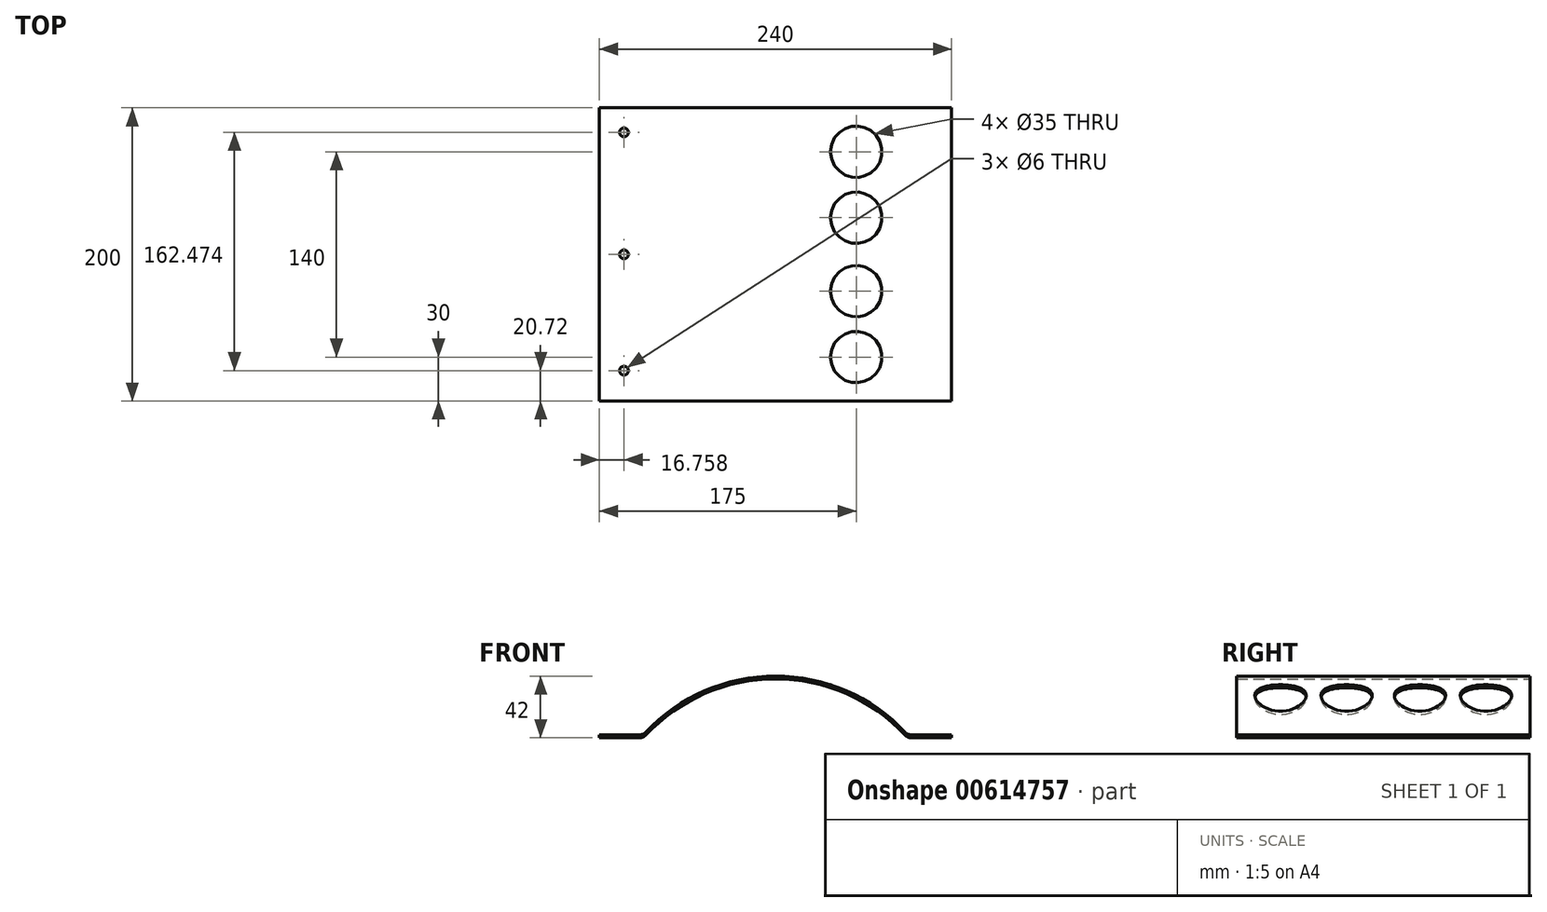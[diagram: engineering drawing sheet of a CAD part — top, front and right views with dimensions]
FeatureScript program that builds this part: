
annotation { "Feature Type Name" : "Feature", "Feature Type Description" : "" }
export const myFeature = defineFeature(function(context is Context, id is Id, definition is map)
    precondition{}
    {
        {
            var Q0;
            Q0=qCreatedBy(makeId("Front.planeOp"),FACE);
            var sketch = newSketch(context, id + "F0", { "sketchPlane" : qUnion([Q0])});
            skLineSegment(sketch, "E0", {"start": v(-120, 0) * mm, "end": v(-120, 2) * mm});
            skLineSegment(sketch, "E1", {"start": v(-120, 2) * mm, "end": v(-90, 2) * mm});
            skLineSegment(sketch, "E2", {"start": v(-90, 2) * mm, "end": v(-90, 0) * mm});
            skLineSegment(sketch, "E3", {"start": v(-90, 0) * mm, "end": v(-120, 0) * mm});
            skLineSegment(sketch, "E4", {"start": v(90, 0) * mm, "end": v(120, 0) * mm});
            skLineSegment(sketch, "E5", {"start": v(120, 0) * mm, "end": v(120, 2) * mm});
            skLineSegment(sketch, "E6", {"start": v(120, 2) * mm, "end": v(90, 2) * mm});
            skLineSegment(sketch, "E7", {"start": v(90, 2) * mm, "end": v(90, 0) * mm});
            skArc(sketch, "E8", {"start": v(90, 0) * mm, "mid": v(0, 40) * mm, "end": v(-90, 0) * mm});
            skArc(sketch, "E9", {"start": v(90, 2) * mm, "mid": v(0, 42) * mm, "end": v(-90, 2) * mm});
            skSolve(sketch);
        }
        {
            var Q0;
            Q0=makeQuery(id+"F0.imprint","IMPRINT",FACE,{"disambiguationData":[TD([[makeQuery(id+"F0.imprint","IMPRINT",EDGE,{"derivedFrom":sQuery(id+"F0.wireOp",EDGE,"E0")}),-1.0]])]});
            var Q1;
            Q1=makeQuery(id+"F0.imprint","IMPRINT",FACE,{"disambiguationData":[TD([[makeQuery(id+"F0.imprint","IMPRINT",EDGE,{"derivedFrom":sQuery(id+"F0.wireOp",EDGE,"E2")}),1.0]])]});
            var Q2;
            Q2=makeQuery(id+"F0.imprint","IMPRINT",FACE,{"disambiguationData":[TD([[makeQuery(id+"F0.imprint","IMPRINT",EDGE,{"derivedFrom":sQuery(id+"F0.wireOp",EDGE,"E4")}),1.0]])]});
            extrude(context, id + "F1", {"entities" : qUnion([Q0, Q1, Q2]), "depth" : 200 * mm, "offsetDistance" : 25 * mm});
        }
        {
            var Q0;
            Q0=makeQuery(id+"F1.opExtrude","SWEPT_FACE",FACE,{"disambiguationData":[OSD([sQuery(id+"F0.wireOp",EDGE,"E1")])]});
            var sketch = newSketch(context, id + "F2", { "sketchPlane" : qUnion([Q0])});
            skCircle(sketch, "E10", {"center": v(-103.24, -100) * mm, "radius": 3 * mm});
            skPoint(sketch, "E10.centerSnap0", {"position": v(-90, -100) * mm});
            skCircle(sketch, "E11", {"center": v(-103.24, -16.8) * mm, "radius": 3 * mm});
            skCircle(sketch, "E12", {"center": v(-103.24, -179.28) * mm, "radius": 3 * mm});
            skCircle(sketch, "E13", {"center": v(55, -30) * mm, "radius": 17.5 * mm});
            skCircle(sketch, "E14", {"center": v(55, -75) * mm, "radius": 17.5 * mm});
            skCircle(sketch, "E15", {"center": v(55, -125) * mm, "radius": 17.5 * mm});
            skCircle(sketch, "E16", {"center": v(55, -170) * mm, "radius": 17.5 * mm});
            skSolve(sketch);
        }
        {
            var Q0;
            Q0=makeQuery(id+"F2.imprint","IMPRINT",FACE,{"disambiguationData":[TD([[makeQuery(id+"F2.imprint","IMPRINT",EDGE,{"derivedFrom":sQuery(id+"F2.wireOp",EDGE,"E11")}),1.0]])]});
            var Q1;
            Q1=makeQuery(id+"F2.imprint","IMPRINT",FACE,{"disambiguationData":[TD([[makeQuery(id+"F2.imprint","IMPRINT",EDGE,{"derivedFrom":sQuery(id+"F2.wireOp",EDGE,"E10")}),1.0]])]});
            var Q2;
            Q2=makeQuery(id+"F2.imprint","IMPRINT",FACE,{"disambiguationData":[TD([[makeQuery(id+"F2.imprint","IMPRINT",EDGE,{"derivedFrom":sQuery(id+"F2.wireOp",EDGE,"E12")}),1.0]])]});
            extrude(context, id + "F3", {"entities" : qUnion([Q0, Q1, Q2]), "operationType" : NewBodyOperationType.REMOVE, "oppositeDirection" : true, "depth" : 25 * mm, "offsetDistance" : 25 * mm});
        }
        {
            var Q0;
            Q0=makeQuery(id+"F2.imprint","IMPRINT",FACE,{"disambiguationData":[TD([[makeQuery(id+"F2.imprint","IMPRINT",EDGE,{"derivedFrom":sQuery(id+"F2.wireOp",EDGE,"E13")}),1.0]])]});
            var Q1;
            Q1=makeQuery(id+"F2.imprint","IMPRINT",FACE,{"disambiguationData":[TD([[makeQuery(id+"F2.imprint","IMPRINT",EDGE,{"derivedFrom":sQuery(id+"F2.wireOp",EDGE,"E14")}),1.0]])]});
            var Q2;
            Q2=makeQuery(id+"F2.imprint","IMPRINT",FACE,{"disambiguationData":[TD([[makeQuery(id+"F2.imprint","IMPRINT",EDGE,{"derivedFrom":sQuery(id+"F2.wireOp",EDGE,"E15")}),1.0]])]});
            var Q3;
            Q3=makeQuery(id+"F2.imprint","IMPRINT",FACE,{"disambiguationData":[TD([[makeQuery(id+"F2.imprint","IMPRINT",EDGE,{"derivedFrom":sQuery(id+"F2.wireOp",EDGE,"E16")}),1.0]])]});
            extrude(context, id + "F4", {"entities" : qUnion([Q0, Q1, Q2, Q3]), "operationType" : NewBodyOperationType.REMOVE, "depth" : 50 * mm, "offsetDistance" : 25 * mm});
        }
        {
            var Q0;
            Q0=makeQuery(id+"F1.opExtrude","SWEPT_EDGE",EDGE,{"disambiguationData":[OSD([sQuery(id+"F0.wireOp",EDGE,"E2"),sQuery(id+"F0.wireOp",EDGE,"E3"),sQuery(id+"F0.wireOp",EDGE,"E8")])]});
            var Q1;
            Q1=makeQuery(id+"F1.opExtrude","SWEPT_EDGE",EDGE,{"disambiguationData":[OSD([sQuery(id+"F0.wireOp",EDGE,"E1"),sQuery(id+"F0.wireOp",EDGE,"E2"),sQuery(id+"F0.wireOp",EDGE,"E9")])]});
            fillet(context, id + "F5", {"entities" : qUnion([Q0, Q1]), "radius" : 5 * mm, "tangentPropagation" : true, "allowEdgeOverflow" : false});
        }
        {
            var Q0;
            Q0=makeQuery(id+"F1.opExtrude","SWEPT_EDGE",EDGE,{"disambiguationData":[OSD([sQuery(id+"F0.wireOp",EDGE,"E6"),sQuery(id+"F0.wireOp",EDGE,"E7"),sQuery(id+"F0.wireOp",EDGE,"E9")])]});
            var Q1;
            Q1=makeQuery(id+"F1.opExtrude","SWEPT_EDGE",EDGE,{"disambiguationData":[OSD([sQuery(id+"F0.wireOp",EDGE,"E4"),sQuery(id+"F0.wireOp",EDGE,"E7"),sQuery(id+"F0.wireOp",EDGE,"E8")])]});
            fillet(context, id + "F6", {"entities" : qUnion([Q0, Q1]), "radius" : 5 * mm, "tangentPropagation" : true, "allowEdgeOverflow" : false});
        }
    });
